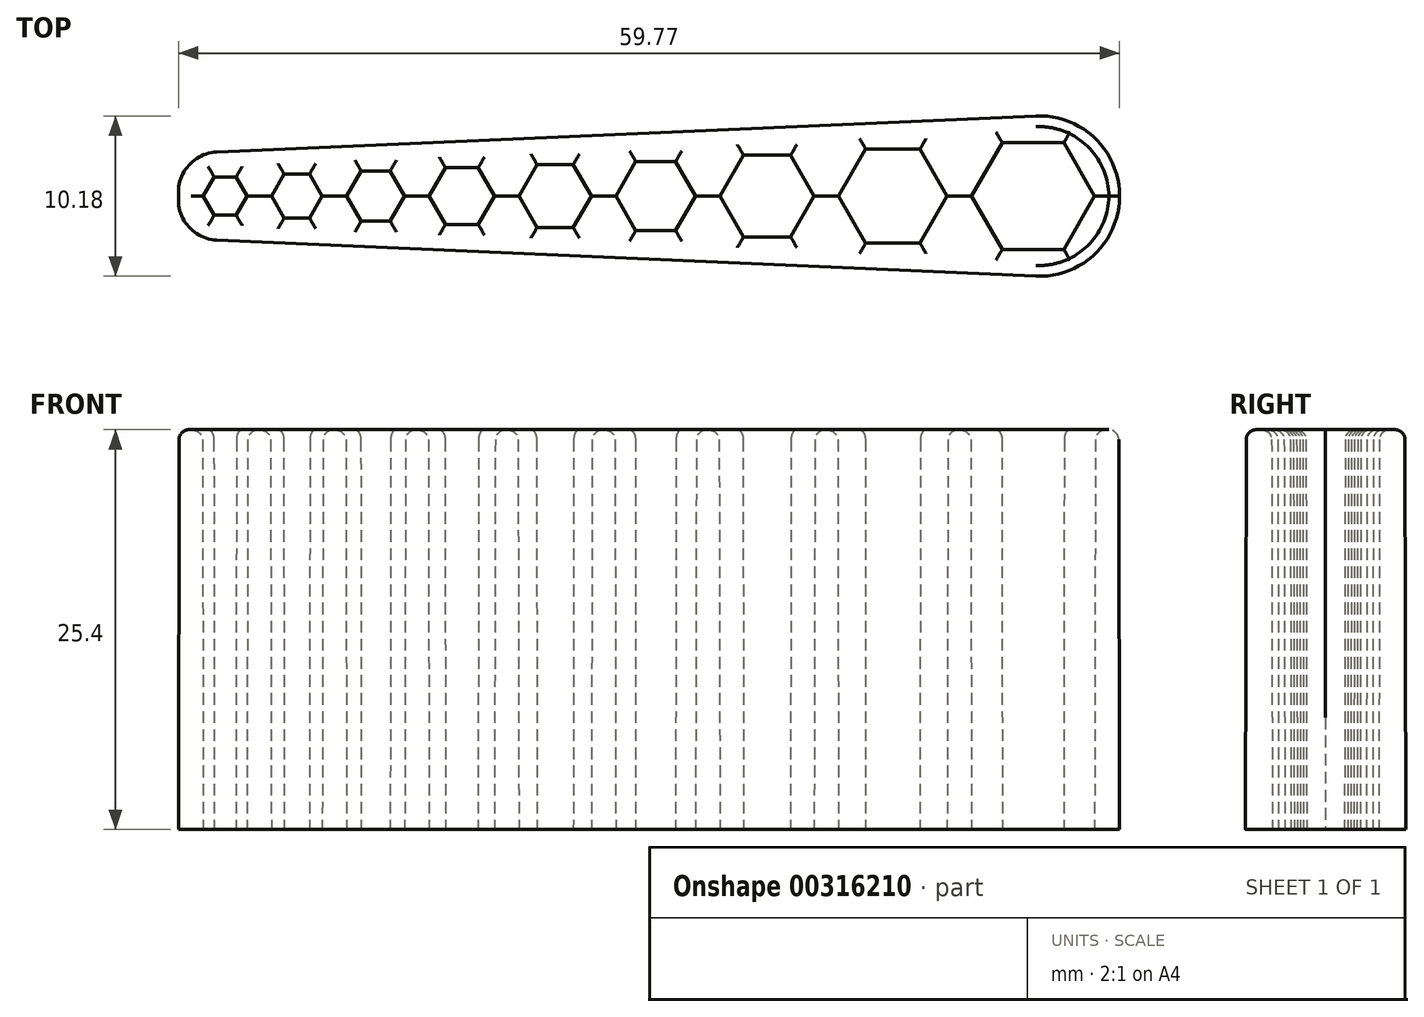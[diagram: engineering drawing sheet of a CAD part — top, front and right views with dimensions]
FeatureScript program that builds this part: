
annotation { "Feature Type Name" : "Feature", "Feature Type Description" : "" }
export const myFeature = defineFeature(function(context is Context, id is Id, definition is map)
    precondition{}
    {
        {
            var Q0;
            Q0=qCreatedBy(makeId("Top.planeOp"),FACE);
            var sketch = newSketch(context, id + "F0", { "sketchPlane" : qUnion([Q0])});
            skCircle(sketch, "E0.cCircle", {"center": v(-59.09, 0) * mm, "radius": 0.64 * mm, "construction": true});
            skLineSegment(sketch, "E0.0", {"start": v(-59.46, 0.63) * mm, "end": v(-58.72, 0.63) * mm});
            skLineSegment(sketch, "E0.1", {"start": v(-58.72, 0.63) * mm, "end": v(-58.36, 0) * mm});
            skLineSegment(sketch, "E0.2", {"start": v(-58.36, 0) * mm, "end": v(-58.72, -0.64) * mm});
            skLineSegment(sketch, "E0.3", {"start": v(-58.72, -0.63) * mm, "end": v(-59.46, -0.63) * mm});
            skLineSegment(sketch, "E0.4", {"start": v(-59.46, -0.64) * mm, "end": v(-59.82, 0) * mm});
            skLineSegment(sketch, "E0.5", {"start": v(-59.82, 0) * mm, "end": v(-59.46, 0.63) * mm});
            skPoint(sketch, "E0.0.midPoint", {"position": v(-59.09, 0.63) * mm});
            skCircle(sketch, "E1.cCircle", {"center": v(-55.4, 0) * mm, "radius": 0.8 * mm, "construction": true});
            skLineSegment(sketch, "E1.0", {"start": v(-55.87, 0.8) * mm, "end": v(-54.95, 0.8) * mm});
            skLineSegment(sketch, "E1.1", {"start": v(-54.95, 0.8) * mm, "end": v(-54.5, 0) * mm});
            skLineSegment(sketch, "E1.2", {"start": v(-54.5, 0) * mm, "end": v(-54.95, -0.8) * mm});
            skLineSegment(sketch, "E1.3", {"start": v(-54.95, -0.8) * mm, "end": v(-55.87, -0.8) * mm});
            skLineSegment(sketch, "E1.4", {"start": v(-55.87, -0.8) * mm, "end": v(-56.32, 0) * mm});
            skLineSegment(sketch, "E1.5", {"start": v(-56.32, 0) * mm, "end": v(-55.87, 0.8) * mm});
            skPoint(sketch, "E1.0.midPoint", {"position": v(-55.4, 0.8) * mm});
            skCircle(sketch, "E2.cCircle", {"center": v(-51.31, 0) * mm, "radius": 1 * mm, "construction": true});
            skLineSegment(sketch, "E2.0", {"start": v(-51.89, 1) * mm, "end": v(-50.74, 1) * mm});
            skLineSegment(sketch, "E2.1", {"start": v(-50.74, 1) * mm, "end": v(-50.17, 0) * mm});
            skLineSegment(sketch, "E2.2", {"start": v(-50.17, 0) * mm, "end": v(-50.74, -1) * mm});
            skLineSegment(sketch, "E2.3", {"start": v(-50.74, -1) * mm, "end": v(-51.89, -1) * mm});
            skLineSegment(sketch, "E2.4", {"start": v(-51.89, -1) * mm, "end": v(-52.46, 0) * mm});
            skLineSegment(sketch, "E2.5", {"start": v(-52.46, 0) * mm, "end": v(-51.89, 1) * mm});
            skPoint(sketch, "E2.0.midPoint", {"position": v(-51.31, 1) * mm});
            skCircle(sketch, "E3.cCircle", {"center": v(-46.76, 0) * mm, "radius": 1.2 * mm, "construction": true});
            skLineSegment(sketch, "E3.0", {"start": v(-47.45, 1.2) * mm, "end": v(-46.07, 1.2) * mm});
            skLineSegment(sketch, "E3.1", {"start": v(-46.07, 1.2) * mm, "end": v(-45.39, 0) * mm});
            skLineSegment(sketch, "E3.2", {"start": v(-45.39, 0) * mm, "end": v(-46.07, -1.2) * mm});
            skLineSegment(sketch, "E3.3", {"start": v(-46.07, -1.2) * mm, "end": v(-47.45, -1.2) * mm});
            skLineSegment(sketch, "E3.4", {"start": v(-47.45, -1.2) * mm, "end": v(-48.14, 0) * mm});
            skLineSegment(sketch, "E3.5", {"start": v(-48.14, 0) * mm, "end": v(-47.45, 1.2) * mm});
            skPoint(sketch, "E3.0.midPoint", {"position": v(-46.76, 1.2) * mm});
            skCircle(sketch, "E4.cCircle", {"center": v(-41.75, 0) * mm, "radius": 1.39 * mm, "construction": true});
            skLineSegment(sketch, "E4.0", {"start": v(-42.55, 1.39) * mm, "end": v(-40.95, 1.39) * mm});
            skLineSegment(sketch, "E4.1", {"start": v(-40.95, 1.39) * mm, "end": v(-40.15, 0) * mm});
            skLineSegment(sketch, "E4.2", {"start": v(-40.15, 0) * mm, "end": v(-40.95, -1.39) * mm});
            skLineSegment(sketch, "E4.3", {"start": v(-40.95, -1.39) * mm, "end": v(-42.55, -1.39) * mm});
            skLineSegment(sketch, "E4.4", {"start": v(-42.55, -1.39) * mm, "end": v(-43.35, 0) * mm});
            skLineSegment(sketch, "E4.5", {"start": v(-43.35, 0) * mm, "end": v(-42.55, 1.39) * mm});
            skPoint(sketch, "E4.0.midPoint", {"position": v(-41.75, 1.39) * mm});
            skCircle(sketch, "E5.cCircle", {"center": v(-36.28, 0) * mm, "radius": 1.59 * mm, "construction": true});
            skLineSegment(sketch, "E5.0", {"start": v(-37.2, 1.59) * mm, "end": v(-35.36, 1.59) * mm});
            skLineSegment(sketch, "E5.1", {"start": v(-35.36, 1.59) * mm, "end": v(-34.45, 0) * mm});
            skLineSegment(sketch, "E5.2", {"start": v(-34.45, 0) * mm, "end": v(-35.36, -1.59) * mm});
            skLineSegment(sketch, "E5.3", {"start": v(-35.36, -1.59) * mm, "end": v(-37.2, -1.59) * mm});
            skLineSegment(sketch, "E5.4", {"start": v(-37.2, -1.59) * mm, "end": v(-38.11, 0) * mm});
            skLineSegment(sketch, "E5.5", {"start": v(-38.11, 0) * mm, "end": v(-37.2, 1.59) * mm});
            skPoint(sketch, "E5.0.midPoint", {"position": v(-36.28, 1.59) * mm});
            skCircle(sketch, "E6.cCircle", {"center": v(-30.35, 0) * mm, "radius": 1.79 * mm, "construction": true});
            skLineSegment(sketch, "E6.0", {"start": v(-31.39, 1.79) * mm, "end": v(-29.32, 1.79) * mm});
            skLineSegment(sketch, "E6.1", {"start": v(-29.32, 1.79) * mm, "end": v(-28.3, 0) * mm});
            skLineSegment(sketch, "E6.2", {"start": v(-28.3, 0) * mm, "end": v(-29.32, -1.79) * mm});
            skLineSegment(sketch, "E6.3", {"start": v(-29.32, -1.79) * mm, "end": v(-31.39, -1.79) * mm});
            skLineSegment(sketch, "E6.4", {"start": v(-31.39, -1.79) * mm, "end": v(-32.42, 0) * mm});
            skLineSegment(sketch, "E6.5", {"start": v(-32.42, 0) * mm, "end": v(-31.39, 1.79) * mm});
            skPoint(sketch, "E6.0.midPoint", {"position": v(-30.35, 1.79) * mm});
            skCircle(sketch, "E7.cCircle", {"center": v(-23.97, 0) * mm, "radius": 1.98 * mm, "construction": true});
            skLineSegment(sketch, "E7.0", {"start": v(-25.11, 1.98) * mm, "end": v(-22.82, 1.98) * mm});
            skLineSegment(sketch, "E7.1", {"start": v(-22.82, 1.98) * mm, "end": v(-21.68, 0) * mm});
            skLineSegment(sketch, "E7.2", {"start": v(-21.68, 0) * mm, "end": v(-22.82, -1.98) * mm});
            skLineSegment(sketch, "E7.3", {"start": v(-22.82, -1.98) * mm, "end": v(-25.11, -1.98) * mm});
            skLineSegment(sketch, "E7.4", {"start": v(-25.11, -1.98) * mm, "end": v(-26.26, 0) * mm});
            skLineSegment(sketch, "E7.5", {"start": v(-26.26, 0) * mm, "end": v(-25.11, 1.98) * mm});
            skPoint(sketch, "E7.0.midPoint", {"position": v(-23.97, 1.98) * mm});
            skCircle(sketch, "E8.cCircle", {"center": v(-16.9, 0) * mm, "radius": 2.38 * mm, "construction": true});
            skLineSegment(sketch, "E8.0", {"start": v(-18.27, 2.38) * mm, "end": v(-15.52, 2.38) * mm});
            skLineSegment(sketch, "E8.1", {"start": v(-15.52, 2.38) * mm, "end": v(-14.15, 0) * mm});
            skLineSegment(sketch, "E8.2", {"start": v(-14.15, 0) * mm, "end": v(-15.52, -2.38) * mm});
            skLineSegment(sketch, "E8.3", {"start": v(-15.52, -2.38) * mm, "end": v(-18.27, -2.38) * mm});
            skLineSegment(sketch, "E8.4", {"start": v(-18.27, -2.38) * mm, "end": v(-19.65, 0) * mm});
            skLineSegment(sketch, "E8.5", {"start": v(-19.65, 0) * mm, "end": v(-18.27, 2.38) * mm});
            skPoint(sketch, "E8.0.midPoint", {"position": v(-16.9, 2.38) * mm});
            skCircle(sketch, "E9.cCircle", {"center": v(-8.9, 0) * mm, "radius": 2.78 * mm, "construction": true});
            skLineSegment(sketch, "E9.0", {"start": v(-10.51, 2.78) * mm, "end": v(-7.3, 2.78) * mm});
            skLineSegment(sketch, "E9.1", {"start": v(-7.3, 2.78) * mm, "end": v(-5.7, 0) * mm});
            skLineSegment(sketch, "E9.2", {"start": v(-5.7, 0) * mm, "end": v(-7.3, -2.78) * mm});
            skLineSegment(sketch, "E9.3", {"start": v(-7.3, -2.78) * mm, "end": v(-10.51, -2.78) * mm});
            skLineSegment(sketch, "E9.4", {"start": v(-10.51, -2.78) * mm, "end": v(-12.11, 0) * mm});
            skLineSegment(sketch, "E9.5", {"start": v(-12.11, 0) * mm, "end": v(-10.51, 2.78) * mm});
            skPoint(sketch, "E9.0.midPoint", {"position": v(-8.9, 2.78) * mm});
            skCircle(sketch, "E10.cCircle", {"center": v(0, 0) * mm, "radius": 3.18 * mm, "construction": true});
            skLineSegment(sketch, "E10.0", {"start": v(-1.83, 3.17) * mm, "end": v(1.83, 3.17) * mm});
            skLineSegment(sketch, "E10.1", {"start": v(1.83, 3.18) * mm, "end": v(3.67, 0) * mm});
            skLineSegment(sketch, "E10.2", {"start": v(3.67, 0) * mm, "end": v(1.83, -3.18) * mm});
            skLineSegment(sketch, "E10.3", {"start": v(1.83, -3.17) * mm, "end": v(-1.83, -3.17) * mm});
            skLineSegment(sketch, "E10.4", {"start": v(-1.83, -3.17) * mm, "end": v(-3.67, 0) * mm});
            skLineSegment(sketch, "E10.5", {"start": v(-3.67, 0) * mm, "end": v(-1.83, 3.17) * mm});
            skPoint(sketch, "E10.0.midPoint", {"position": v(0, 3.17) * mm});
            skLineSegment(sketch, "E11", {"start": v(-61.86, 2.56) * mm, "end": v(-61.86, 0) * mm});
            skLineSegment(sketch, "E12", {"start": v(-61.86, 2.56) * mm, "end": v(5.7, 5.54) * mm});
            skLineSegment(sketch, "E13", {"start": v(5.7, 5.54) * mm, "end": v(5.7, 0) * mm});
            skLineSegment(sketch, "E14.MirrorCS", {"start": v(-61.86, -2.56) * mm, "end": v(-61.86, 0) * mm});
            skLineSegment(sketch, "E15.MirrorCS", {"start": v(-61.86, -2.56) * mm, "end": v(5.7, -5.54) * mm});
            skLineSegment(sketch, "E16.MirrorCS", {"start": v(5.7, -5.54) * mm, "end": v(5.7, 0) * mm});
            skLineSegment(sketch, "E17", {"start": v(-54.5, 0) * mm, "end": v(-54.5, 2.89) * mm});
            skLineSegment(sketch, "E18.MirrorCS", {"start": v(-54.5, 0) * mm, "end": v(-54.5, -2.89) * mm});
            skSolve(sketch);
        }
        {
            var Q0;
            Q0=makeQuery(id+"F0.imprint","IMPRINT",FACE,{"disambiguationData":[TD([[makeQuery(id+"F0.imprint","IMPRINT",EDGE,{"derivedFrom":sQuery(id+"F0.wireOp",EDGE,"E2.0")}),1.0]])]});
            extrude(context, id + "F1", {"entities" : qUnion([Q0]), "depth" : 25.4 * mm});
        }
        {
            var Q0;
            Q0=makeQuery(id+"F1.opExtrude","CAP_FACE",FACE,{"disambiguationData":[OSD([sQuery(id+"F0.wireOp",EDGE,"E0.0"),sQuery(id+"F0.wireOp",EDGE,"E0.1"),sQuery(id+"F0.wireOp",EDGE,"E0.2"),sQuery(id+"F0.wireOp",EDGE,"E0.3"),sQuery(id+"F0.wireOp",EDGE,"E0.4"),sQuery(id+"F0.wireOp",EDGE,"E0.5"),sQuery(id+"F0.wireOp",EDGE,"E1.0"),sQuery(id+"F0.wireOp",EDGE,"E1.1"),sQuery(id+"F0.wireOp",EDGE,"E1.2"),sQuery(id+"F0.wireOp",EDGE,"E1.3"),sQuery(id+"F0.wireOp",EDGE,"E1.4"),sQuery(id+"F0.wireOp",EDGE,"E1.5"),sQuery(id+"F0.wireOp",EDGE,"E2.0"),sQuery(id+"F0.wireOp",EDGE,"E2.1"),sQuery(id+"F0.wireOp",EDGE,"E2.2"),sQuery(id+"F0.wireOp",EDGE,"E2.3"),sQuery(id+"F0.wireOp",EDGE,"E2.4"),sQuery(id+"F0.wireOp",EDGE,"E2.5"),sQuery(id+"F0.wireOp",EDGE,"E3.0"),sQuery(id+"F0.wireOp",EDGE,"E3.1"),sQuery(id+"F0.wireOp",EDGE,"E3.2"),sQuery(id+"F0.wireOp",EDGE,"E3.3"),sQuery(id+"F0.wireOp",EDGE,"E3.4"),sQuery(id+"F0.wireOp",EDGE,"E3.5"),sQuery(id+"F0.wireOp",EDGE,"E4.0"),sQuery(id+"F0.wireOp",EDGE,"E4.1"),sQuery(id+"F0.wireOp",EDGE,"E4.2"),sQuery(id+"F0.wireOp",EDGE,"E4.3"),sQuery(id+"F0.wireOp",EDGE,"E4.4"),sQuery(id+"F0.wireOp",EDGE,"E4.5"),sQuery(id+"F0.wireOp",EDGE,"E5.0"),sQuery(id+"F0.wireOp",EDGE,"E5.1"),sQuery(id+"F0.wireOp",EDGE,"E5.2"),sQuery(id+"F0.wireOp",EDGE,"E5.3"),sQuery(id+"F0.wireOp",EDGE,"E5.4"),sQuery(id+"F0.wireOp",EDGE,"E5.5"),sQuery(id+"F0.wireOp",EDGE,"E6.0"),sQuery(id+"F0.wireOp",EDGE,"E6.1"),sQuery(id+"F0.wireOp",EDGE,"E6.2"),sQuery(id+"F0.wireOp",EDGE,"E6.3"),sQuery(id+"F0.wireOp",EDGE,"E6.4"),sQuery(id+"F0.wireOp",EDGE,"E6.5"),sQuery(id+"F0.wireOp",EDGE,"E7.0"),sQuery(id+"F0.wireOp",EDGE,"E7.1"),sQuery(id+"F0.wireOp",EDGE,"E7.2"),sQuery(id+"F0.wireOp",EDGE,"E7.3"),sQuery(id+"F0.wireOp",EDGE,"E7.4"),sQuery(id+"F0.wireOp",EDGE,"E7.5"),sQuery(id+"F0.wireOp",EDGE,"E8.0"),sQuery(id+"F0.wireOp",EDGE,"E8.1"),sQuery(id+"F0.wireOp",EDGE,"E8.2"),sQuery(id+"F0.wireOp",EDGE,"E8.3"),sQuery(id+"F0.wireOp",EDGE,"E8.4"),sQuery(id+"F0.wireOp",EDGE,"E8.5"),sQuery(id+"F0.wireOp",EDGE,"E9.0"),sQuery(id+"F0.wireOp",EDGE,"E9.1"),sQuery(id+"F0.wireOp",EDGE,"E9.2"),sQuery(id+"F0.wireOp",EDGE,"E9.3"),sQuery(id+"F0.wireOp",EDGE,"E9.4"),sQuery(id+"F0.wireOp",EDGE,"E9.5"),sQuery(id+"F0.wireOp",EDGE,"E10.0"),sQuery(id+"F0.wireOp",EDGE,"E10.1"),sQuery(id+"F0.wireOp",EDGE,"E10.2"),sQuery(id+"F0.wireOp",EDGE,"E10.3"),sQuery(id+"F0.wireOp",EDGE,"E10.4"),sQuery(id+"F0.wireOp",EDGE,"E10.5"),sQuery(id+"F0.wireOp",EDGE,"E11"),sQuery(id+"F0.wireOp",EDGE,"E12"),sQuery(id+"F0.wireOp",EDGE,"E13"),sQuery(id+"F0.wireOp",EDGE,"E14.MirrorCS"),sQuery(id+"F0.wireOp",EDGE,"E15.MirrorCS"),sQuery(id+"F0.wireOp",EDGE,"E16.MirrorCS")])],"isStart":false});
            chamfer(context, id + "F2", {"entities" : qUnion([Q0]), "chamferType" : ChamferType.OFFSET_ANGLE, "width" : 0.25 * mm, "oppositeDirection" : false, "angle" : 89.9 * degree, "tangentPropagation" : true});
        }
        {
            var Q0;
            Q0=makeQuery(id+"F2.opChamfer","BLEND_EDGE",EDGE,{"blendedFrom":[makeQuery(id+"F1.opExtrude","CAP_EDGE",EDGE,{"disambiguationData":[OSD([sQuery(id+"F0.wireOp",EDGE,"E11"),sQuery(id+"F0.wireOp",EDGE,"E14.MirrorCS")])],"isStart":false}),makeQuery(id+"F1.opExtrude","CAP_EDGE",EDGE,{"disambiguationData":[OSD([sQuery(id+"F0.wireOp",EDGE,"E12")])],"isStart":false})],"blendedInto":[]});
            var Q1;
            Q1=makeQuery(id+"F2.opChamfer","BLEND_EDGE",EDGE,{"blendedFrom":[makeQuery(id+"F1.opExtrude","CAP_EDGE",EDGE,{"disambiguationData":[OSD([sQuery(id+"F0.wireOp",EDGE,"E11"),sQuery(id+"F0.wireOp",EDGE,"E14.MirrorCS")])],"isStart":false}),makeQuery(id+"F1.opExtrude","CAP_EDGE",EDGE,{"disambiguationData":[OSD([sQuery(id+"F0.wireOp",EDGE,"E15.MirrorCS")])],"isStart":false})],"blendedInto":[]});
            var Q2;
            Q2=makeQuery(id+"F2.opChamfer","BLEND_EDGE",EDGE,{"blendedFrom":[makeQuery(id+"F1.opExtrude","CAP_EDGE",EDGE,{"disambiguationData":[OSD([sQuery(id+"F0.wireOp",EDGE,"E12")])],"isStart":false}),makeQuery(id+"F1.opExtrude","CAP_EDGE",EDGE,{"disambiguationData":[OSD([sQuery(id+"F0.wireOp",EDGE,"E17"),sQuery(id+"F0.wireOp",EDGE,"E18.MirrorCS")])],"isStart":false})],"blendedInto":[]});
            var Q3;
            Q3=makeQuery(id+"F2.opChamfer","BLEND_EDGE",EDGE,{"blendedFrom":[makeQuery(id+"F1.opExtrude","CAP_EDGE",EDGE,{"disambiguationData":[OSD([sQuery(id+"F0.wireOp",EDGE,"E15.MirrorCS")])],"isStart":false}),makeQuery(id+"F1.opExtrude","CAP_EDGE",EDGE,{"disambiguationData":[OSD([sQuery(id+"F0.wireOp",EDGE,"E17"),sQuery(id+"F0.wireOp",EDGE,"E18.MirrorCS")])],"isStart":false})],"blendedInto":[]});
            fillet(context, id + "F3", {"entities" : qUnion([Q0, Q1, Q2, Q3]), "radius" : 2.54 * mm, "tangentPropagation" : true, "allowEdgeOverflow" : false});
        }
        {
            var Q0;
            Q0=makeQuery(id+"F2.opChamfer","BLEND_EDGE",EDGE,{"blendedFrom":[makeQuery(id+"F1.opExtrude","CAP_EDGE",EDGE,{"disambiguationData":[OSD([sQuery(id+"F0.wireOp",EDGE,"E12")])],"isStart":false}),makeQuery(id+"F1.opExtrude","CAP_EDGE",EDGE,{"disambiguationData":[OSD([sQuery(id+"F0.wireOp",EDGE,"E13"),sQuery(id+"F0.wireOp",EDGE,"E16.MirrorCS")])],"isStart":false})],"blendedInto":[]});
            var Q1;
            Q1=makeQuery(id+"F2.opChamfer","BLEND_EDGE",EDGE,{"blendedFrom":[makeQuery(id+"F1.opExtrude","CAP_EDGE",EDGE,{"disambiguationData":[OSD([sQuery(id+"F0.wireOp",EDGE,"E13"),sQuery(id+"F0.wireOp",EDGE,"E16.MirrorCS")])],"isStart":false}),makeQuery(id+"F1.opExtrude","CAP_EDGE",EDGE,{"disambiguationData":[OSD([sQuery(id+"F0.wireOp",EDGE,"E15.MirrorCS")])],"isStart":false})],"blendedInto":[]});
            fillet(context, id + "F4", {"entities" : qUnion([Q0, Q1]), "radius" : 5.08 * mm, "tangentPropagation" : true, "allowEdgeOverflow" : false});
        }
        {
            var Q0;
            Q0=makeQuery(id+"F1.opExtrude","CAP_FACE",FACE,{"disambiguationData":[OSD([sQuery(id+"F0.wireOp",EDGE,"E0.0"),sQuery(id+"F0.wireOp",EDGE,"E0.1"),sQuery(id+"F0.wireOp",EDGE,"E0.2"),sQuery(id+"F0.wireOp",EDGE,"E0.3"),sQuery(id+"F0.wireOp",EDGE,"E0.4"),sQuery(id+"F0.wireOp",EDGE,"E0.5"),sQuery(id+"F0.wireOp",EDGE,"E1.0"),sQuery(id+"F0.wireOp",EDGE,"E1.1"),sQuery(id+"F0.wireOp",EDGE,"E1.2"),sQuery(id+"F0.wireOp",EDGE,"E1.3"),sQuery(id+"F0.wireOp",EDGE,"E1.4"),sQuery(id+"F0.wireOp",EDGE,"E1.5"),sQuery(id+"F0.wireOp",EDGE,"E2.0"),sQuery(id+"F0.wireOp",EDGE,"E2.1"),sQuery(id+"F0.wireOp",EDGE,"E2.2"),sQuery(id+"F0.wireOp",EDGE,"E2.3"),sQuery(id+"F0.wireOp",EDGE,"E2.4"),sQuery(id+"F0.wireOp",EDGE,"E2.5"),sQuery(id+"F0.wireOp",EDGE,"E3.0"),sQuery(id+"F0.wireOp",EDGE,"E3.1"),sQuery(id+"F0.wireOp",EDGE,"E3.2"),sQuery(id+"F0.wireOp",EDGE,"E3.3"),sQuery(id+"F0.wireOp",EDGE,"E3.4"),sQuery(id+"F0.wireOp",EDGE,"E3.5"),sQuery(id+"F0.wireOp",EDGE,"E4.0"),sQuery(id+"F0.wireOp",EDGE,"E4.1"),sQuery(id+"F0.wireOp",EDGE,"E4.2"),sQuery(id+"F0.wireOp",EDGE,"E4.3"),sQuery(id+"F0.wireOp",EDGE,"E4.4"),sQuery(id+"F0.wireOp",EDGE,"E4.5"),sQuery(id+"F0.wireOp",EDGE,"E5.0"),sQuery(id+"F0.wireOp",EDGE,"E5.1"),sQuery(id+"F0.wireOp",EDGE,"E5.2"),sQuery(id+"F0.wireOp",EDGE,"E5.3"),sQuery(id+"F0.wireOp",EDGE,"E5.4"),sQuery(id+"F0.wireOp",EDGE,"E5.5"),sQuery(id+"F0.wireOp",EDGE,"E6.0"),sQuery(id+"F0.wireOp",EDGE,"E6.1"),sQuery(id+"F0.wireOp",EDGE,"E6.2"),sQuery(id+"F0.wireOp",EDGE,"E6.3"),sQuery(id+"F0.wireOp",EDGE,"E6.4"),sQuery(id+"F0.wireOp",EDGE,"E6.5"),sQuery(id+"F0.wireOp",EDGE,"E7.0"),sQuery(id+"F0.wireOp",EDGE,"E7.1"),sQuery(id+"F0.wireOp",EDGE,"E7.2"),sQuery(id+"F0.wireOp",EDGE,"E7.3"),sQuery(id+"F0.wireOp",EDGE,"E7.4"),sQuery(id+"F0.wireOp",EDGE,"E7.5"),sQuery(id+"F0.wireOp",EDGE,"E8.0"),sQuery(id+"F0.wireOp",EDGE,"E8.1"),sQuery(id+"F0.wireOp",EDGE,"E8.2"),sQuery(id+"F0.wireOp",EDGE,"E8.3"),sQuery(id+"F0.wireOp",EDGE,"E8.4"),sQuery(id+"F0.wireOp",EDGE,"E8.5"),sQuery(id+"F0.wireOp",EDGE,"E9.0"),sQuery(id+"F0.wireOp",EDGE,"E9.1"),sQuery(id+"F0.wireOp",EDGE,"E9.2"),sQuery(id+"F0.wireOp",EDGE,"E9.3"),sQuery(id+"F0.wireOp",EDGE,"E9.4"),sQuery(id+"F0.wireOp",EDGE,"E9.5"),sQuery(id+"F0.wireOp",EDGE,"E10.0"),sQuery(id+"F0.wireOp",EDGE,"E10.1"),sQuery(id+"F0.wireOp",EDGE,"E10.2"),sQuery(id+"F0.wireOp",EDGE,"E10.3"),sQuery(id+"F0.wireOp",EDGE,"E10.4"),sQuery(id+"F0.wireOp",EDGE,"E10.5"),sQuery(id+"F0.wireOp",EDGE,"E11"),sQuery(id+"F0.wireOp",EDGE,"E12"),sQuery(id+"F0.wireOp",EDGE,"E13"),sQuery(id+"F0.wireOp",EDGE,"E14.MirrorCS"),sQuery(id+"F0.wireOp",EDGE,"E15.MirrorCS"),sQuery(id+"F0.wireOp",EDGE,"E16.MirrorCS")])],"isStart":false});
            fillet(context, id + "F5", {"entities" : qUnion([Q0]), "radius" : 0.64 * mm, "tangentPropagation" : true, "allowEdgeOverflow" : false});
        }
    });
